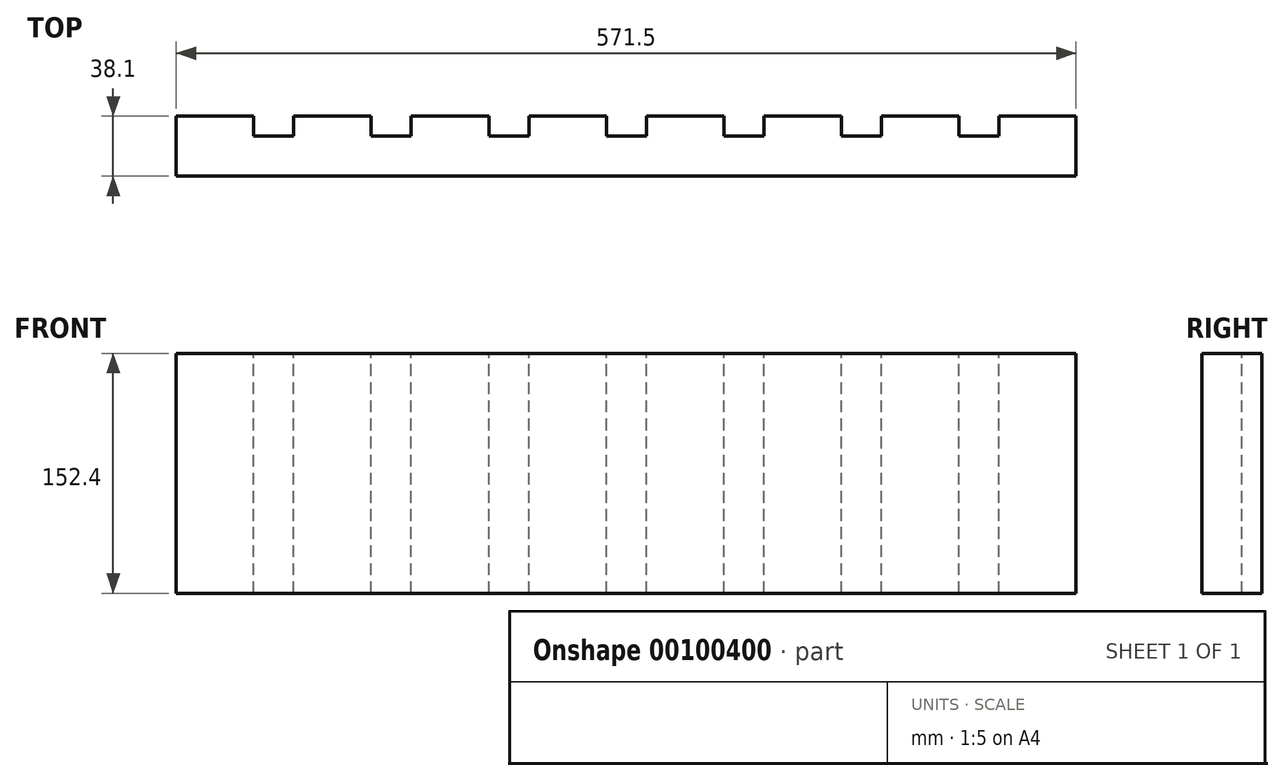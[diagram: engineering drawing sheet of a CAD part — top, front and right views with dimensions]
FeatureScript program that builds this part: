
annotation { "Feature Type Name" : "Feature", "Feature Type Description" : "" }
export const myFeature = defineFeature(function(context is Context, id is Id, definition is map)
    precondition{}
    {
        {
            var Q0;
            Q0=qCreatedBy(makeId("Right.planeOp"),FACE);
            var sketch = newSketch(context, id + "F0", { "sketchPlane" : qUnion([Q0])});
            skLineSegment(sketch, "E0.bottom", {"start": v(-19.05, 76.2) * mm, "end": v(19.05, 76.2) * mm});
            skLineSegment(sketch, "E0.top", {"start": v(-19.05, -76.2) * mm, "end": v(19.05, -76.2) * mm});
            skLineSegment(sketch, "E0.left", {"start": v(-19.05, 76.2) * mm, "end": v(-19.05, -76.2) * mm});
            skLineSegment(sketch, "E0.right", {"start": v(19.05, 76.2) * mm, "end": v(19.05, -76.2) * mm});
            skPoint(sketch, "E0.middle", {"position": v(0, 0) * mm});
            skSolve(sketch);
        }
        {
            var Q0;
            Q0 = qSketchRegion(id + "F0", true);
            extrude(context, id + "F1", {"entities" : qUnion([Q0]), "endBound" : BoundingType.SYMMETRIC, "depth" : 571.5 * mm});
        }
        {
            var Q0;
            Q0=makeQuery(id+"F1.opExtrude","SWEPT_FACE",FACE,{"disambiguationData":[OSD([sQuery(id+"F0.wireOp",EDGE,"E0.bottom")])]});
            var sketch = newSketch(context, id + "F2", { "sketchPlane" : qUnion([Q0])});
            skLineSegment(sketch, "E1.0", {"start": v(285.75, 19.05) * mm, "end": v(-285.75, 19.05) * mm, "construction": true});
            skLineSegment(sketch, "E2.0", {"start": v(285.75, 6.35) * mm, "end": v(-285.75, 6.35) * mm, "construction": true});
            skLineSegment(sketch, "E3.0", {"start": v(-285.75, -19.05) * mm, "end": v(-285.75, 19.05) * mm, "construction": true});
            skLineSegment(sketch, "E4.0", {"start": v(-236.5, -19.05) * mm, "end": v(-236.5, 19.05) * mm, "construction": true});
            skLineSegment(sketch, "E5.bottom", {"start": v(-236.5, 6.35) * mm, "end": v(-211.1, 6.35) * mm});
            skLineSegment(sketch, "E5.top", {"start": v(-236.5, 19.05) * mm, "end": v(-211.1, 19.05) * mm});
            skLineSegment(sketch, "E5.left", {"start": v(-236.5, 6.35) * mm, "end": v(-236.5, 19.05) * mm});
            skLineSegment(sketch, "E5.right", {"start": v(-211.1, 6.35) * mm, "end": v(-211.1, 19.05) * mm});
            skLineSegment(sketch, "E6.1.0.0", {"start": v(-161.86, 19.05) * mm, "end": v(-136.46, 19.05) * mm});
            skLineSegment(sketch, "E6.1.0.1", {"start": v(-161.86, 6.35) * mm, "end": v(-136.46, 6.35) * mm});
            skLineSegment(sketch, "E6.1.0.2", {"start": v(-136.46, 6.35) * mm, "end": v(-136.46, 19.05) * mm});
            skLineSegment(sketch, "E6.1.0.3", {"start": v(-161.86, 6.35) * mm, "end": v(-161.86, 19.05) * mm});
            skLineSegment(sketch, "E6.2.0.0", {"start": v(-87.22, 19.05) * mm, "end": v(-61.82, 19.05) * mm});
            skLineSegment(sketch, "E6.2.0.1", {"start": v(-87.22, 6.35) * mm, "end": v(-61.82, 6.35) * mm});
            skLineSegment(sketch, "E6.2.0.2", {"start": v(-61.82, 6.35) * mm, "end": v(-61.82, 19.05) * mm});
            skLineSegment(sketch, "E6.2.0.3", {"start": v(-87.22, 6.35) * mm, "end": v(-87.22, 19.05) * mm});
            skLineSegment(sketch, "E6.3.0.0", {"start": v(-12.57, 19.05) * mm, "end": v(12.83, 19.05) * mm});
            skLineSegment(sketch, "E6.3.0.1", {"start": v(-12.57, 6.35) * mm, "end": v(12.83, 6.35) * mm});
            skLineSegment(sketch, "E6.3.0.2", {"start": v(12.83, 6.35) * mm, "end": v(12.83, 19.05) * mm});
            skLineSegment(sketch, "E6.3.0.3", {"start": v(-12.57, 6.35) * mm, "end": v(-12.57, 19.05) * mm});
            skLineSegment(sketch, "E6.4.0.0", {"start": v(62.07, 19.05) * mm, "end": v(87.47, 19.05) * mm});
            skLineSegment(sketch, "E6.4.0.1", {"start": v(62.07, 6.35) * mm, "end": v(87.47, 6.35) * mm});
            skLineSegment(sketch, "E6.4.0.2", {"start": v(87.47, 6.35) * mm, "end": v(87.47, 19.05) * mm});
            skLineSegment(sketch, "E6.4.0.3", {"start": v(62.07, 6.35) * mm, "end": v(62.07, 19.05) * mm});
            skLineSegment(sketch, "E6.5.0.0", {"start": v(136.72, 19.05) * mm, "end": v(162.12, 19.05) * mm});
            skLineSegment(sketch, "E6.5.0.1", {"start": v(136.72, 6.35) * mm, "end": v(162.12, 6.35) * mm});
            skLineSegment(sketch, "E6.5.0.2", {"start": v(162.12, 6.35) * mm, "end": v(162.12, 19.05) * mm});
            skLineSegment(sketch, "E6.5.0.3", {"start": v(136.72, 6.35) * mm, "end": v(136.72, 19.05) * mm});
            skLineSegment(sketch, "E6.6.0.0", {"start": v(211.36, 19.05) * mm, "end": v(236.76, 19.05) * mm});
            skLineSegment(sketch, "E6.6.0.1", {"start": v(211.36, 6.35) * mm, "end": v(236.76, 6.35) * mm});
            skLineSegment(sketch, "E6.6.0.2", {"start": v(236.76, 6.35) * mm, "end": v(236.76, 19.05) * mm});
            skLineSegment(sketch, "E6.6.0.3", {"start": v(211.36, 6.35) * mm, "end": v(211.36, 19.05) * mm});
            skLineSegment(sketch, "E6.direction1", {"start": v(-236.5, 19.05) * mm, "end": v(-161.86, 19.05) * mm, "construction": true});
            skSolve(sketch);
        }
        {
            var Q0;
            Q0 = qSketchRegion(id + "F2", true);
            extrude(context, id + "F3", {"entities" : qUnion([Q0]), "operationType" : NewBodyOperationType.REMOVE, "endBound" : BoundingType.THROUGH_ALL, "oppositeDirection" : true, "depth" : 25.4 * mm});
        }
    });
